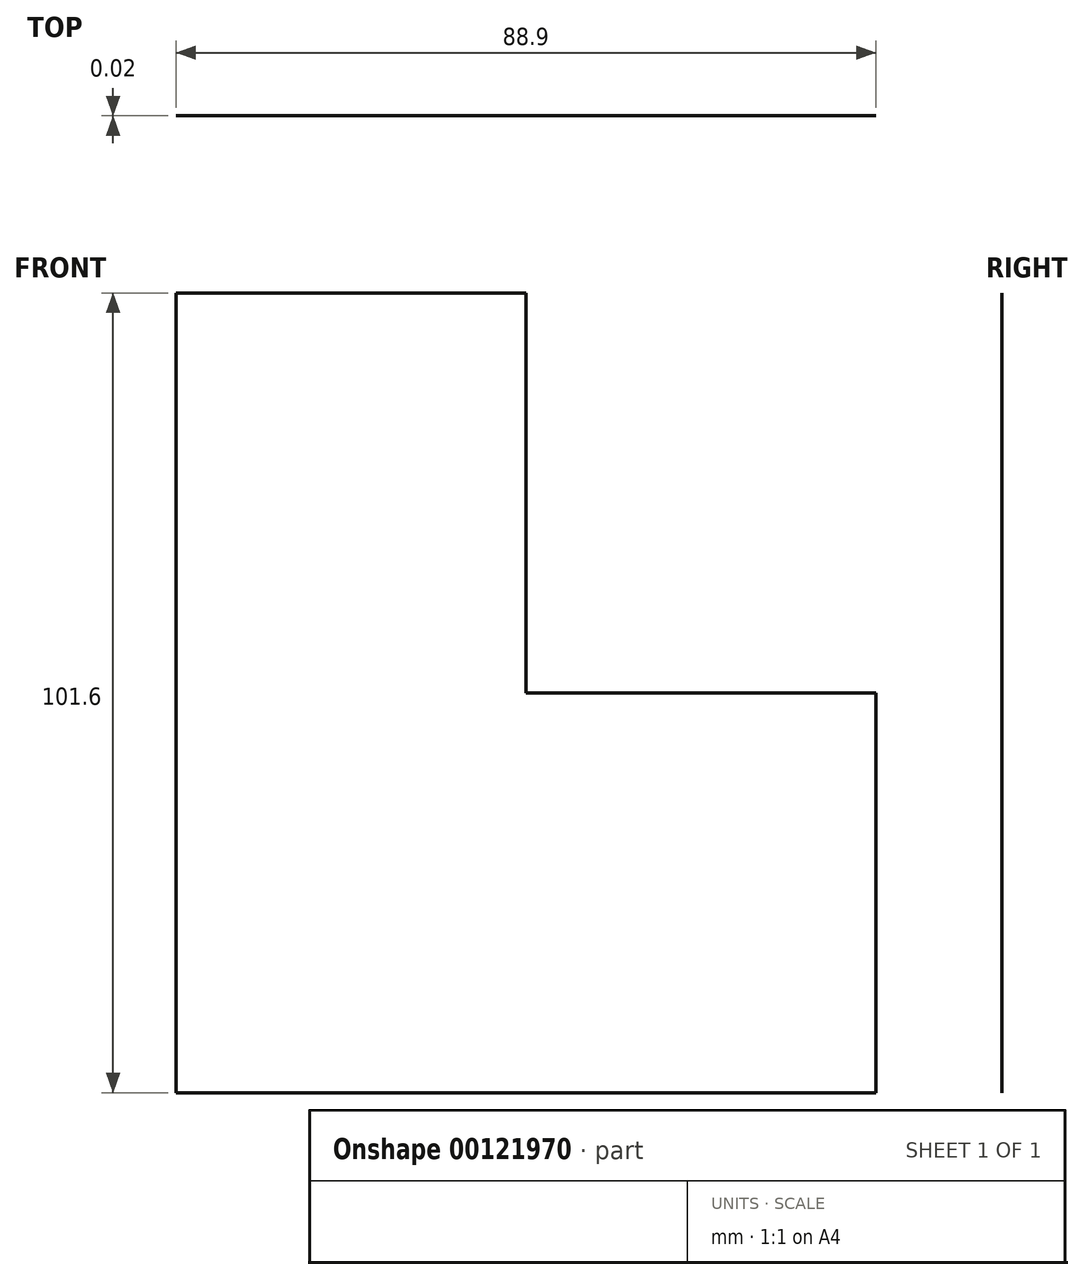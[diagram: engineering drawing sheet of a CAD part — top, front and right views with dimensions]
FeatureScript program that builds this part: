
annotation { "Feature Type Name" : "Feature", "Feature Type Description" : "" }
export const myFeature = defineFeature(function(context is Context, id is Id, definition is map)
    precondition{}
    {
        {
            var Q0;
            Q0=qCreatedBy(makeId("Front.planeOp"),FACE);
            var sketch = newSketch(context, id + "F0", { "sketchPlane" : qUnion([Q0])});
            skLineSegment(sketch, "E0.bottom", {"start": v(0, 0) * mm, "end": v(88.9, 0) * mm});
            skLineSegment(sketch, "E0.top", {"start": v(0, 101.6) * mm, "end": v(88.9, 101.6) * mm});
            skLineSegment(sketch, "E0.left", {"start": v(0, 0) * mm, "end": v(0, 101.6) * mm});
            skLineSegment(sketch, "E0.right", {"start": v(88.9, 0) * mm, "end": v(88.9, 101.6) * mm});
            skLineSegment(sketch, "E1.bottom", {"start": v(88.9, 101.6) * mm, "end": v(44.45, 101.6) * mm});
            skLineSegment(sketch, "E1.top", {"start": v(88.9, 50.8) * mm, "end": v(44.45, 50.8) * mm});
            skLineSegment(sketch, "E1.left", {"start": v(88.9, 101.6) * mm, "end": v(88.9, 50.8) * mm});
            skLineSegment(sketch, "E1.right", {"start": v(44.45, 101.6) * mm, "end": v(44.45, 50.8) * mm});
            skSolve(sketch);
        }
        {
            var Q0;
            Q0=makeQuery(id+"F0.imprint","IMPRINT",FACE,{"disambiguationData":[TD([[makeQuery(id+"F0.imprint","IMPRINT",EDGE,{"derivedFrom":sQuery(id+"F0.wireOp",EDGE,"E0.bottom")}),1.0]])]});
            extrude(context, id + "F1", {"entities" : qUnion([Q0]), "depth" : 1 / 50.8 * mm});
        }
    });
